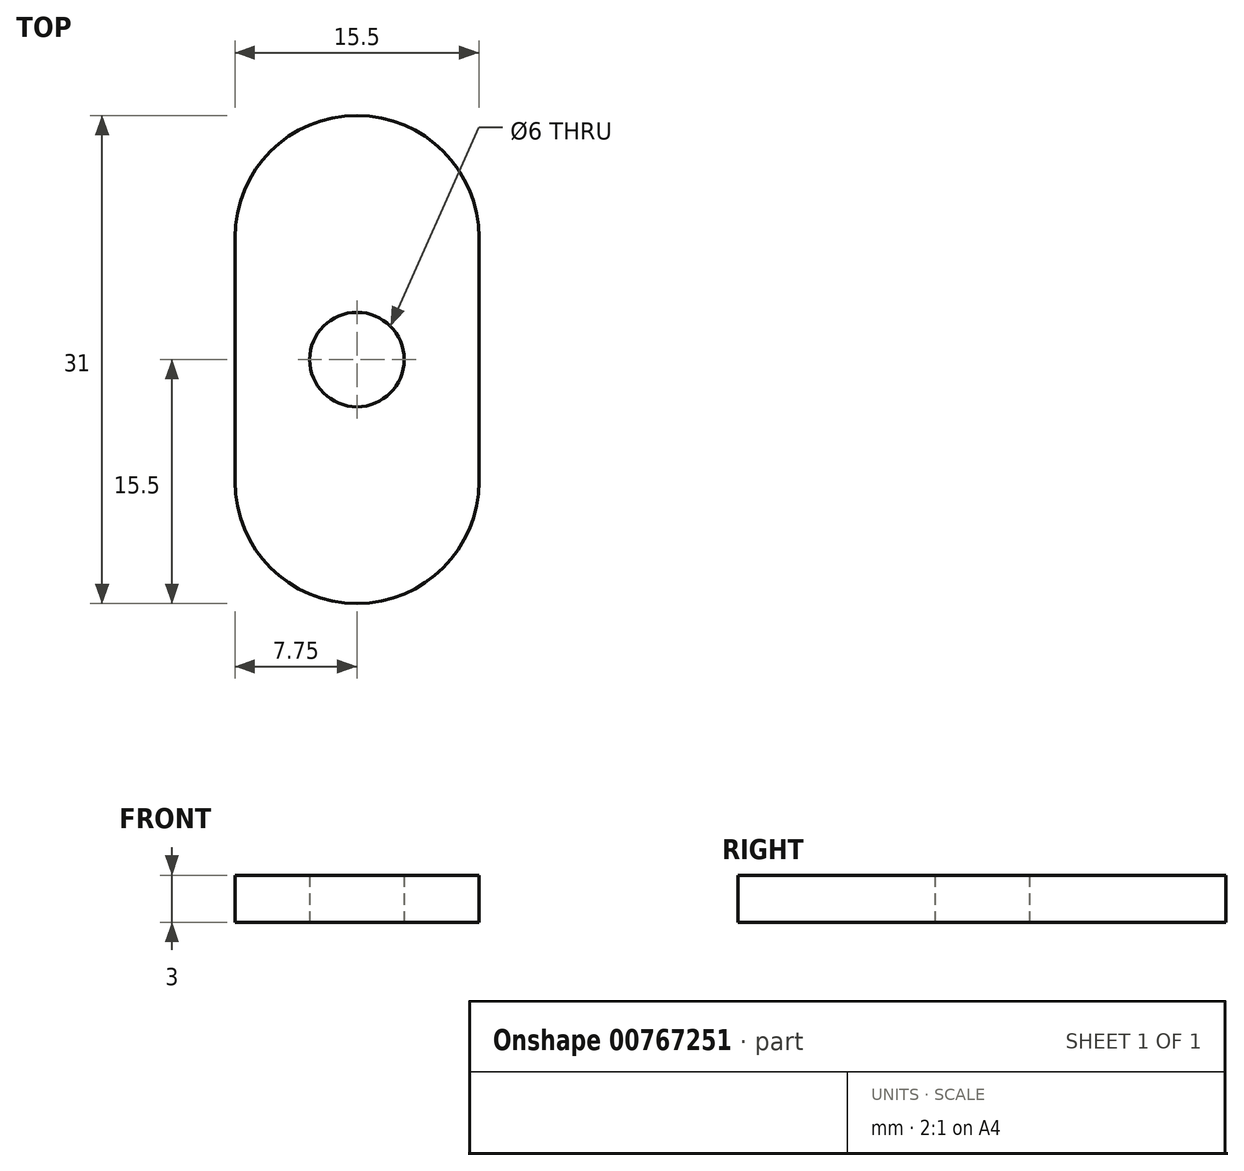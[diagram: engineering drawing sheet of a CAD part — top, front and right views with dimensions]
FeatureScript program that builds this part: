
annotation { "Feature Type Name" : "Feature", "Feature Type Description" : "" }
export const myFeature = defineFeature(function(context is Context, id is Id, definition is map)
    precondition{}
    {
        {
            var Q0;
            Q0=qCreatedBy(makeId("Top.planeOp"),FACE);
            var sketch = newSketch(context, id + "F0", { "sketchPlane" : qUnion([Q0])});
            skLineSegment(sketch, "E0.bottom", {"start": v(7.75, -7.75) * mm, "end": v(-7.75, -7.75) * mm});
            skLineSegment(sketch, "E0.top", {"start": v(7.75, 7.75) * mm, "end": v(-7.75, 7.75) * mm});
            skLineSegment(sketch, "E0.left", {"start": v(7.75, -7.75) * mm, "end": v(7.75, 7.75) * mm});
            skLineSegment(sketch, "E0.right", {"start": v(-7.75, -7.75) * mm, "end": v(-7.75, 7.75) * mm});
            skPoint(sketch, "E0.middle", {"position": v(0, 0) * mm});
            skCircle(sketch, "E1", {"center": v(0, 0) * mm, "radius": 3 * mm});
            skArc(sketch, "E2", {"start": v(7.75, 7.75) * mm, "mid": v(0, 15.5) * mm, "end": v(-7.75, 7.75) * mm});
            skArc(sketch, "E3", {"start": v(-7.75, -7.75) * mm, "mid": v(0, -15.5) * mm, "end": v(7.75, -7.75) * mm});
            skSolve(sketch);
        }
        {
            var Q0;
            Q0 = qSketchRegion(id + "F0", true);
            extrude(context, id + "F1", {"entities" : qUnion([Q0]), "depth" : 3 * mm, "offsetDistance" : 25 * mm});
        }
    });
